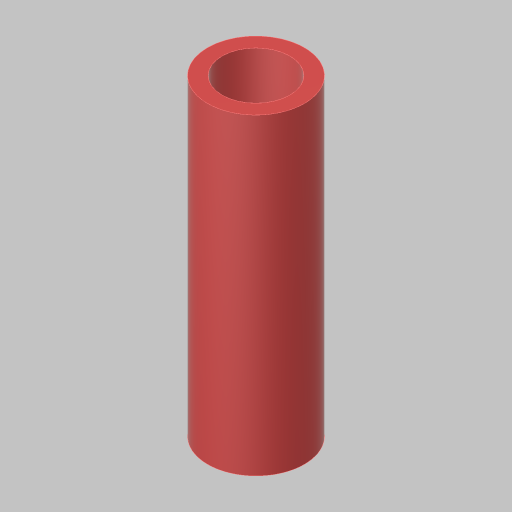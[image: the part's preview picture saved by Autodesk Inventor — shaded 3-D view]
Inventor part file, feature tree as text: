
AUTODESK INVENTOR PART (.ipt)
format: ipt  version: 2023.5 (Build 275446000, 446)  size: 96,256 bytes
history: native  units: in
note: dims shown in document units (in); Inventor stores cm internally (conversion verified against a paired STEP export)
features: extrude x1, sketch x1
ambient origin geometry x8: Origin, YZ Plane, XZ Plane, XY Plane, X Axis, Y Axis, Z Axis, Center Point
bodies: Solid1 (feature_tree)
feature tree (2):
  extrude  "Extrusion1"  Depth=2.68in
  sketch  "Sketch1"  dims[d0=0.58in d1=0.125in d2=2.68in d3=0.0in]
